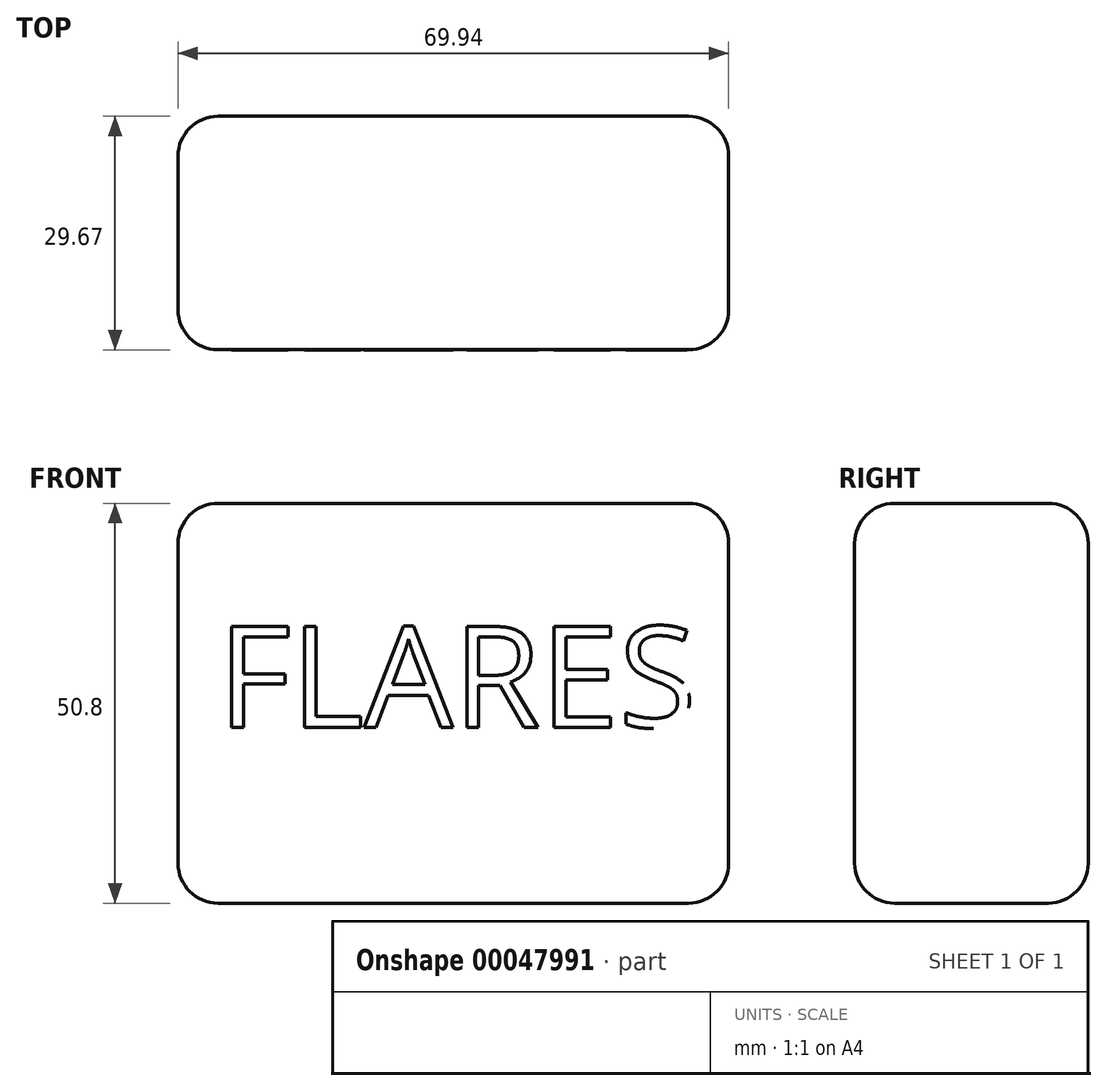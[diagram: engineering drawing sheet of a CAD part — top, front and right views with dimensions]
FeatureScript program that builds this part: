
annotation { "Feature Type Name" : "Feature", "Feature Type Description" : "" }
export const myFeature = defineFeature(function(context is Context, id is Id, definition is map)
    precondition{}
    {
        {
            var Q0;
            Q0=qCreatedBy(makeId("Top.planeOp"),FACE);
            var sketch = newSketch(context, id + "F0", { "sketchPlane" : qUnion([Q0])});
            skLineSegment(sketch, "E0.rect.bottom", {"start": v(34.97, -14.83) * mm, "end": v(-34.97, -14.83) * mm});
            skLineSegment(sketch, "E0.rect.top", {"start": v(34.97, 14.83) * mm, "end": v(-34.97, 14.83) * mm});
            skLineSegment(sketch, "E0.rect.left", {"start": v(34.97, -14.83) * mm, "end": v(34.97, 14.83) * mm});
            skLineSegment(sketch, "E0.rect.right", {"start": v(-34.97, -14.83) * mm, "end": v(-34.97, 14.83) * mm});
            skPoint(sketch, "E0.rect.middle", {"position": v(0, 0) * mm});
            skSolve(sketch);
        }
        {
            var Q0;
            Q0 = qSketchRegion(id + "F0", true);
            extrude(context, id + "F1", {"entities" : qUnion([Q0]), "depth" : 25.4 * mm, "hasSecondDirection" : true, "secondDirectionOppositeDirection" : true, "secondDirectionDepth" : 25.4 * mm});
        }
        {
            var Q0;
            Q0=makeQuery(id+"F1.opExtrude","SWEPT_FACE",FACE,{"disambiguationData":[OSD([sQuery(id+"F0.wireOp",EDGE,"E0.rect.top")])]});
            var Q1;
            Q1=makeQuery(id+"F1.opExtrude","SWEPT_FACE",FACE,{"disambiguationData":[OSD([sQuery(id+"F0.wireOp",EDGE,"E0.rect.bottom")])]});
            var Q2;
            Q2=makeQuery(id+"F1.opExtrude","CAP_EDGE",EDGE,{"disambiguationData":[OSD([sQuery(id+"F0.wireOp",EDGE,"E0.rect.left")])],"isStart":false});
            var Q3;
            Q3=makeQuery(id+"F1.opExtrude","CAP_EDGE",EDGE,{"disambiguationData":[OSD([sQuery(id+"F0.wireOp",EDGE,"E0.rect.right")])],"isStart":false});
            var Q4;
            Q4=makeQuery(id+"F1.opExtrude","CAP_EDGE",EDGE,{"disambiguationData":[OSD([sQuery(id+"F0.wireOp",EDGE,"E0.rect.right")])],"isStart":true});
            var Q5;
            Q5=makeQuery(id+"F1.opExtrude","CAP_EDGE",EDGE,{"disambiguationData":[OSD([sQuery(id+"F0.wireOp",EDGE,"E0.rect.left")])],"isStart":true});
            fillet(context, id + "F2", {"entities" : qUnion([Q0, Q1, Q2, Q3, Q4, Q5]), "radius" : 5.08 * mm, "tangentPropagation" : true, "allowEdgeOverflow" : false});
        }
        {
            var Q0;
            Q0=makeQuery(id+"F1.opExtrude","SWEPT_FACE",FACE,{"disambiguationData":[OSD([sQuery(id+"F0.wireOp",EDGE,"E0.rect.bottom")])]});
            var sketch = newSketch(context, id + "F3", { "sketchPlane" : qUnion([Q0])});
            skText(sketch, "E1", { "text": "FLARES", "fontName": "OpenSans-Regular.ttf"});
            const initialGuessF3  = {"E1": [-0.0299, -0.00304, 1, 0, 0.0129]};
            skSetInitialGuess(sketch, initialGuessF3);
            skSolve(sketch);
        }
        {
            var Q0;
            Q0 = qSketchRegion(id + "F3", true);
            extrude(context, id + "F4", {"entities" : qUnion([Q0]), "operationType" : NewBodyOperationType.ADD, "depth" : 1 / 203.2 * mm});
        }
    });
